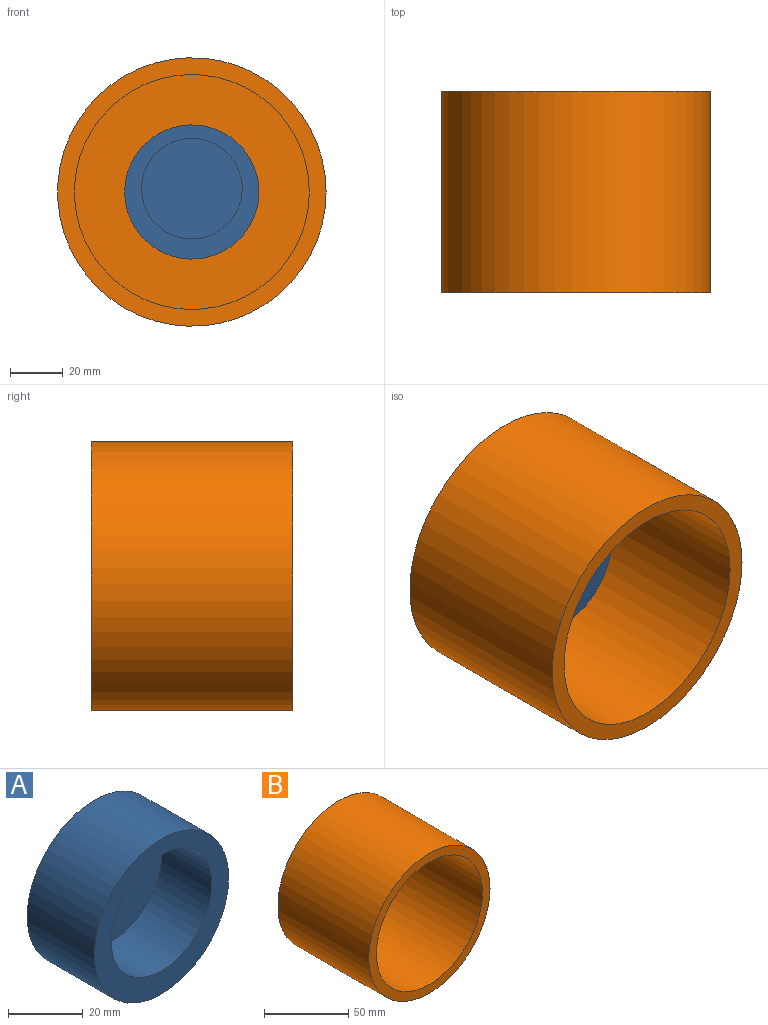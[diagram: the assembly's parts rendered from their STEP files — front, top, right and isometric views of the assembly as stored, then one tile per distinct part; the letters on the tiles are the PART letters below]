
ASSEMBLY  parts=2 mates=1
PART A: 5 faces, bbox 50.8x25.4x50.8 mm
  f0: cylinder r=19.05mm len=38.1mm, axis (0,1,0), area 2280.2mm2, adj f2,f4
  f1: cylinder r=25.4mm len=50.8mm, axis (0,1,0), area 4053.7mm2, adj f2,f3
  f2: plane 50.8x50.8mm, normal (0,-1,0), area 886.7mm2, adj f0,f1
  f3: plane 50.8x50.8mm, normal (0,1,0), area 2026.8mm2, adj f1
  f4: plane 38.1x38.1mm, normal (0,-1,0), area 1140.1mm2, adj f0
PART B: 5 faces, bbox 101.6x76.2x101.6 mm
  f0: cylinder r=44.45mm len=88.9mm, axis (0,1,0), area 19508.2mm2, adj f2,f4
  f1: cylinder r=50.8mm len=101.6mm, axis (0,1,0), area 24322mm2, adj f2,f3
  f2: plane 101.6x101.6mm, normal (0,-1,0), area 1900.2mm2, adj f0,f1
  f3: plane 101.6x101.6mm, normal (0,1,0), area 8107.3mm2, adj f1
  f4: plane 88.9x88.9mm, normal (0,-1,0), area 6207.2mm2, adj f0
PLACE A t=(24.23,3.7,-14.2)mm
PLACE B t=(24.23,10.05,-15.44)mm
MATE slider A.f1 <-> B.f0  axis (0,1,0) through (24.23,3.7,-15.44)mm
